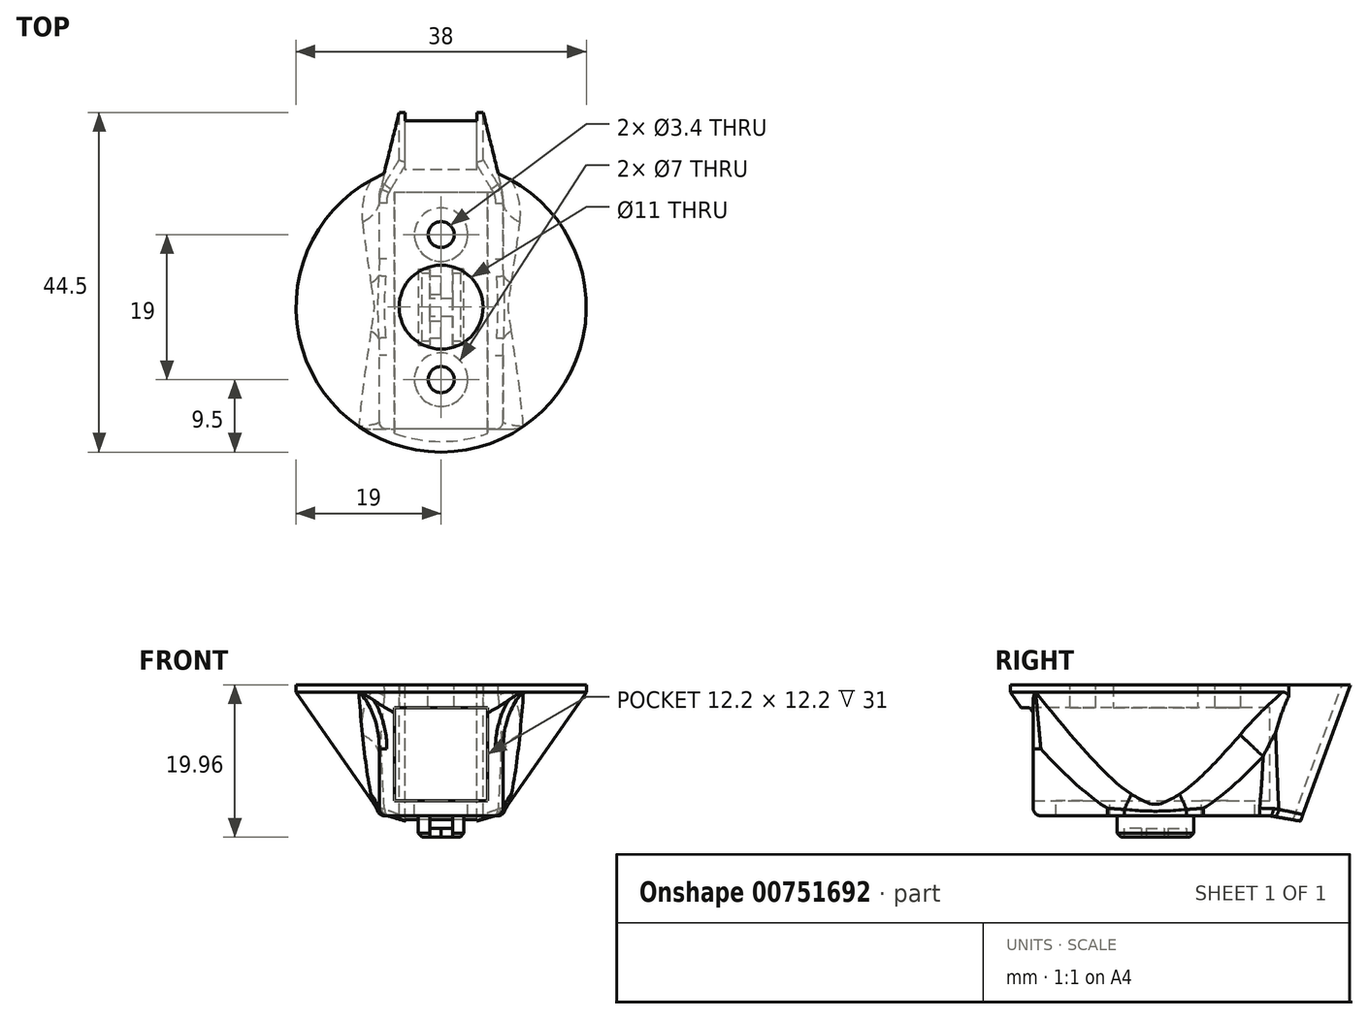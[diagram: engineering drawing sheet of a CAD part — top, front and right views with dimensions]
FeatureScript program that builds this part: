
annotation { "Feature Type Name" : "Feature", "Feature Type Description" : "" }
export const myFeature = defineFeature(function(context is Context, id is Id, definition is map)
    precondition{}
    {
        {
            var Q0;
            Q0=qCreatedBy(makeId("Front.planeOp"),FACE);
            var sketch = newSketch(context, id + "F0", { "sketchPlane" : qUnion([Q0])});
            skLineSegment(sketch, "E0", {"start": v(0, 1) * mm, "end": v(0, -16.2) * mm});
            skLineSegment(sketch, "E1", {"start": v(0, -16.2) * mm, "end": v(-7.76, -16.2) * mm});
            skLineSegment(sketch, "E2", {"start": v(-7.76, -16.2) * mm, "end": v(-19, 0) * mm});
            skLineSegment(sketch, "E3", {"start": v(-19, 0) * mm, "end": v(-19, 0.96) * mm});
            skLineSegment(sketch, "E4", {"start": v(-19, 0.96) * mm, "end": v(0, 1) * mm});
            skSolve(sketch);
        }
        {
            var Q0;
            Q0 = qSketchRegion(id + "F0", true);
            var Q1;
            Q1=sQuery(id+"F0.wireOp",EDGE,"E0");
            revolve(context, id + "F1", {"surfaceOperationType" : NewSurfaceOperationType.NEW, "entities" : qUnion([Q0]), "axis" : qUnion([Q1]), "revolveType" : RevolveType.FULL});
        }
        {
            var Q0;
            Q0=qCreatedBy(makeId("Top.planeOp"),FACE);
            var sketch = newSketch(context, id + "F2", { "sketchPlane" : qUnion([Q0])});
            skCircle(sketch, "E5", {"center": v(0, 9.5) * mm, "radius": 1.7 * mm});
            skCircle(sketch, "E6.MirrorC", {"center": v(0, -9.5) * mm, "radius": 1.7 * mm});
            skSolve(sketch);
        }
        {
            var Q0;
            Q0=qCreatedBy(makeId("Front.planeOp"),FACE);
            var sketch = newSketch(context, id + "F3", { "sketchPlane" : qUnion([Q0])});
            skLineSegment(sketch, "E7.bottom", {"start": v(6.1, -14.2) * mm, "end": v(-6.1, -14.2) * mm});
            skLineSegment(sketch, "E7.top", {"start": v(6.1, -2) * mm, "end": v(-6.1, -2) * mm});
            skLineSegment(sketch, "E7.left", {"start": v(6.1, -14.2) * mm, "end": v(6.1, -2) * mm});
            skLineSegment(sketch, "E7.right", {"start": v(-6.1, -14.2) * mm, "end": v(-6.1, -2) * mm});
            skPoint(sketch, "E7.middle", {"position": v(0, -8.1) * mm});
            skLineSegment(sketch, "E8.0", {"start": v(8.1, 0) * mm, "end": v(-8.1, 0) * mm});
            skLineSegment(sketch, "E8.1", {"start": v(8.1, -16.2) * mm, "end": v(8.1, 0) * mm});
            skLineSegment(sketch, "E8.2", {"start": v(8.1, -16.2) * mm, "end": v(-8.1, -16.2) * mm});
            skLineSegment(sketch, "E8.3", {"start": v(-8.1, -16.2) * mm, "end": v(-8.1, 0) * mm});
            skSolve(sketch);
        }
        {
            var Q0;
            Q0=makeQuery(id+"F3.imprint","IMPRINT",FACE,{"disambiguationData":[TD([[makeQuery(id+"F3.imprint","IMPRINT",EDGE,{"derivedFrom":sQuery(id+"F3.wireOp",EDGE,"E7.bottom")}),1.0]])]});
            extrude(context, id + "F4", {"entities" : qUnion([Q0]), "operationType" : NewBodyOperationType.ADD, "depth" : 16 * mm, "offsetDistance" : 25 * mm, "hasSecondDirection" : true, "secondDirectionOppositeDirection" : true, "secondDirectionDepth" : 15 * mm});
        }
        {
            var Q0;
            Q0=qCreatedBy(makeId("Front.planeOp"),FACE);
            var sketch = newSketch(context, id + "F5", { "sketchPlane" : qUnion([Q0])});
            skLineSegment(sketch, "E9.bottom", {"start": v(6.1, -14.2) * mm, "end": v(-6.1, -14.2) * mm});
            skLineSegment(sketch, "E9.top", {"start": v(6.1, -2) * mm, "end": v(-6.1, -2) * mm});
            skLineSegment(sketch, "E9.left", {"start": v(6.1, -14.2) * mm, "end": v(6.1, -2) * mm});
            skLineSegment(sketch, "E9.right", {"start": v(-6.1, -14.2) * mm, "end": v(-6.1, -2) * mm});
            skPoint(sketch, "E9.middle", {"position": v(0, -8.1) * mm});
            skSolve(sketch);
        }
        {
            var Q0;
            Q0 = qSketchRegion(id + "F5", true);
            extrude(context, id + "F6", {"entities" : qUnion([Q0]), "operationType" : NewBodyOperationType.REMOVE, "oppositeDirection" : true, "depth" : 25 * mm, "offsetDistance" : 25 * mm, "hasSecondDirection" : true, "secondDirectionOppositeDirection" : false, "secondDirectionDepth" : 25 * mm});
        }
        {
            var Q0;
            Q0 = qSketchRegion(id + "F2", true);
            var Q1;
            Q1=sQuery(id+"F2.wireOp",EDGE,"E5");
            var Q2;
            Q2=sQuery(id+"F2.wireOp",EDGE,"E6.MirrorC");
            extrude(context, id + "F7", {"entities" : qUnion([Q0]), "operationType" : NewBodyOperationType.REMOVE, "surfaceEntities" : qUnion([Q1, Q2]), "oppositeDirection" : true, "depth" : 25 * mm, "offsetDistance" : 25 * mm, "hasSecondDirection" : true, "secondDirectionOppositeDirection" : false, "secondDirectionDepth" : 25 * mm});
        }
        {
            var Q0;
            Q0=qCreatedBy(makeId("Top.planeOp"),FACE);
            var sketch = newSketch(context, id + "F8", { "sketchPlane" : qUnion([Q0])});
            skCircle(sketch, "E10", {"center": v(0, 9.5) * mm, "radius": 3.5 * mm});
            skCircle(sketch, "E11", {"center": v(0, -9.5) * mm, "radius": 3.5 * mm});
            skSolve(sketch);
        }
        {
            var Q0;
            Q0 = qSketchRegion(id + "F8", true);
            extrude(context, id + "F9", {"entities" : qUnion([Q0]), "operationType" : NewBodyOperationType.REMOVE, "oppositeDirection" : true, "depth" : 25 * mm, "offsetDistance" : 25 * mm, "hasSecondDirection" : true, "secondDirectionOppositeDirection" : true, "secondDirectionDepth" : 8.9 * mm});
        }
        {
            var Q0;
            Q0=qCreatedBy(makeId("Top.planeOp"),FACE);
            var sketch = newSketch(context, id + "F10", { "sketchPlane" : qUnion([Q0])});
            skCircle(sketch, "E12", {"center": v(0, 0) * mm, "radius": 5.5 * mm});
            skSolve(sketch);
        }
        {
            var Q0;
            Q0 = qSketchRegion(id + "F10", true);
            extrude(context, id + "F11", {"entities" : qUnion([Q0]), "operationType" : NewBodyOperationType.REMOVE, "depth" : 25 * mm, "offsetDistance" : 25 * mm, "hasSecondDirection" : true, "secondDirectionOppositeDirection" : true, "secondDirectionDepth" : 5 * mm});
        }
        {
            var Q0;
            Q0=makeQuery(id+"F4.opExtrude","CAP_EDGE",EDGE,{"disambiguationData":[OSD([sQuery(id+"F3.wireOp",EDGE,"E8.2")])],"isStart":true});
            cPlane(context, id + "F12", {"entities" : qUnion([Q0]), "cplaneType" : CPlaneType.LINE_ANGLE, "offset" : 25 * mm, "angle" : 20 * degree, "width" : 150 * mm, "height" : 150 * mm});
        }
        {
            var Q0;
            Q0=qCreatedBy(id+"F12.planeOp",FACE);
            cPlane(context, id + "F13", {"entities" : qUnion([Q0]), "cplaneType" : CPlaneType.OFFSET, "offset" : 4 * mm, "oppositeDirection" : true, "width" : 150 * mm, "height" : 150 * mm});
        }
        {
            var Q0;
            Q0=makeQuery(id+"F4.opExtrude","CAP_FACE",FACE,{"disambiguationData":[OSD([sQuery(id+"F3.wireOp",EDGE,"E7.bottom"),sQuery(id+"F3.wireOp",EDGE,"E7.top"),sQuery(id+"F3.wireOp",EDGE,"E7.left"),sQuery(id+"F3.wireOp",EDGE,"E7.right"),sQuery(id+"F3.wireOp",EDGE,"E8.0"),sQuery(id+"F3.wireOp",EDGE,"E8.1"),sQuery(id+"F3.wireOp",EDGE,"E8.2"),sQuery(id+"F3.wireOp",EDGE,"E8.3")])],"isStart":true});
            cPlane(context, id + "F14", {"entities" : qUnion([Q0]), "cplaneType" : CPlaneType.OFFSET, "offset" : 0 * mm, "width" : 150 * mm, "height" : 150 * mm});
        }
        {
            var Q0;
            Q0=qCreatedBy(id+"F13.planeOp",FACE);
            var sketch = newSketch(context, id + "F15", { "sketchPlane" : qUnion([Q0])});
            skLineSegment(sketch, "E13.bottom", {"start": v(-5.5, -9.38) * mm, "end": v(5.5, -9.38) * mm});
            skLineSegment(sketch, "E13.top", {"start": v(-5.5, 9.62) * mm, "end": v(5.5, 9.62) * mm});
            skLineSegment(sketch, "E13.left", {"start": v(-5.5, -9.38) * mm, "end": v(-5.5, 9.62) * mm});
            skLineSegment(sketch, "E13.right", {"start": v(5.5, -9.38) * mm, "end": v(5.5, 9.62) * mm});
            skPoint(sketch, "E13.middle", {"position": v(0, 0.72) * mm});
            skSolve(sketch);
        }
        {
            var Q0;
            Q0=qCreatedBy(id+"F14.planeOp",FACE);
            var sketch = newSketch(context, id + "F16", { "sketchPlane" : qUnion([Q0])});
            skLineSegment(sketch, "E14.bottom", {"start": v(-8.1, -16.2) * mm, "end": v(8.1, -16.2) * mm});
            skLineSegment(sketch, "E14.top", {"start": v(-8.1, 1.14) * mm, "end": v(8.1, 1.14) * mm});
            skLineSegment(sketch, "E14.left", {"start": v(-8.1, -16.2) * mm, "end": v(-8.1, 1.14) * mm});
            skLineSegment(sketch, "E14.right", {"start": v(8.1, -16.2) * mm, "end": v(8.1, 1.14) * mm});
            skSolve(sketch);
        }
        {
            var Q1;
            Q1 = qSketchRegion(id + "F15", true);
            var Q2;
            Q2 = qSketchRegion(id + "F16", true);
            loft(context, id + "F17", {"operationType" : NewBodyOperationType.ADD, "sheetProfilesArray" : [{ "sheetProfileEntities" : qUnion([Q1]) }, { "sheetProfileEntities" : qUnion([Q2]) }]});
        }
        {
            var Q0;
            Q0=qCreatedBy(makeId("Front.planeOp"),FACE);
            var sketch = newSketch(context, id + "F18", { "sketchPlane" : qUnion([Q0])});
            skLineSegment(sketch, "E15.bottom", {"start": v(19.79, 8.07) * mm, "end": v(-19.65, 8.07) * mm});
            skLineSegment(sketch, "E15.top", {"start": v(19.79, 0.96) * mm, "end": v(-19.65, 0.96) * mm});
            skLineSegment(sketch, "E15.left", {"start": v(19.79, 8.07) * mm, "end": v(19.79, 0.96) * mm});
            skLineSegment(sketch, "E15.right", {"start": v(-19.65, 8.07) * mm, "end": v(-19.65, 0.96) * mm});
            skSolve(sketch);
        }
        {
            var Q0;
            Q0 = qSketchRegion(id + "F18", true);
            extrude(context, id + "F19", {"entities" : qUnion([Q0]), "operationType" : NewBodyOperationType.REMOVE, "endBound" : BoundingType.SYMMETRIC, "oppositeDirection" : true, "depth" : 54.4 * mm, "offsetDistance" : 25 * mm});
        }
        {
            var Q0;
            Q0=qCreatedBy(id+"F13.planeOp",FACE);
            var sketch = newSketch(context, id + "F20", { "sketchPlane" : qUnion([Q0])});
            skPoint(sketch, "E16.middle", {"position": v(0, 0) * mm});
            skPoint(sketch, "E17.middle", {"position": v(0, -0.26) * mm});
            skLineSegment(sketch, "E18.bottom", {"start": v(-4.7, -11.6) * mm, "end": v(4.7, -11.6) * mm});
            skLineSegment(sketch, "E18.top", {"start": v(-4.7, 11.6) * mm, "end": v(4.7, 11.6) * mm});
            skLineSegment(sketch, "E18.left", {"start": v(-4.7, -11.6) * mm, "end": v(-4.7, 11.6) * mm});
            skLineSegment(sketch, "E18.right", {"start": v(4.7, -11.6) * mm, "end": v(4.7, 11.6) * mm});
            skSolve(sketch);
        }
        {
            var Q0;
            Q0 = qSketchRegion(id + "F20", true);
            extrude(context, id + "F21", {"entities" : qUnion([Q0]), "operationType" : NewBodyOperationType.REMOVE, "depth" : 1 * mm, "offsetDistance" : 25 * mm});
        }
        {
            var Q0;
            Q0=makeQuery(id+"F17.boolean.opBoolean","MERGE",EDGE,{"derivedFrom":[makeQuery(id+"F4.opExtrude","CAP_EDGE",EDGE,{"disambiguationData":[OSD([sQuery(id+"F3.wireOp",EDGE,"E8.1")])],"isStart":true}),makeQuery(id+"F17.opLoft","MID_CAP_EDGE",EDGE,{"disambiguationData":[OSD([sQuery(id+"F16.wireOp",EDGE,"E14.bottom"),sQuery(id+"F16.wireOp",EDGE,"E14.top"),sQuery(id+"F16.wireOp",EDGE,"E14.left")])],"capPos":1.0})]});
            var Q1;
            Q1=makeQuery(id+"F4.boolean.opBoolean","INTERSECT",EDGE,{"derivedFrom":[makeQuery(id+"F1.opRevolve","SWEPT_FACE",FACE,{"disambiguationData":[OSD([sQuery(id+"F0.wireOp",EDGE,"E2")])]}),makeQuery(id+"F4.opExtrude","SWEPT_FACE",FACE,{"disambiguationData":[OSD([sQuery(id+"F3.wireOp",EDGE,"E8.1")])]})]});
            var Q2;
            Q2=makeQuery(id+"F4.boolean.opBoolean","INTERSECT",EDGE,{"derivedFrom":[makeQuery(id+"F1.opRevolve","SWEPT_FACE",FACE,{"disambiguationData":[OSD([sQuery(id+"F0.wireOp",EDGE,"E2")])]}),makeQuery(id+"F4.opExtrude","SWEPT_FACE",FACE,{"disambiguationData":[OSD([sQuery(id+"F3.wireOp",EDGE,"E8.3")])]})]});
            var Q3;
            Q3=makeQuery(id+"F17.boolean.opBoolean","MERGE",EDGE,{"derivedFrom":[makeQuery(id+"F4.opExtrude","CAP_EDGE",EDGE,{"disambiguationData":[OSD([sQuery(id+"F3.wireOp",EDGE,"E8.3")])],"isStart":true}),makeQuery(id+"F17.opLoft","MID_CAP_EDGE",EDGE,{"disambiguationData":[OSD([sQuery(id+"F16.wireOp",EDGE,"E14.bottom"),sQuery(id+"F16.wireOp",EDGE,"E14.top"),sQuery(id+"F16.wireOp",EDGE,"E14.right")])],"capPos":1.0})]});
            fillet(context, id + "F22", {"entities" : qUnion([Q0, Q1, Q2, Q3]), "radius" : 5 * mm, "tangentPropagation" : true, "allowEdgeOverflow" : false});
        }
        {
            var Q0;
            Q0=makeQuery(id+"F4.opExtrude","SWEPT_EDGE",EDGE,{"disambiguationData":[OSD([sQuery(id+"F3.wireOp",EDGE,"E8.1"),sQuery(id+"F3.wireOp",EDGE,"E8.2")])]});
            var Q1;
            Q1=makeQuery(id+"F22.opFillet","BLEND_EDGE",EDGE,{"blendedFrom":[makeQuery(id+"F4.boolean.opBoolean","INTERSECT",EDGE,{"derivedFrom":[makeQuery(id+"F1.opRevolve","SWEPT_FACE",FACE,{"disambiguationData":[OSD([sQuery(id+"F0.wireOp",EDGE,"E2")])]}),makeQuery(id+"F4.opExtrude","SWEPT_FACE",FACE,{"disambiguationData":[OSD([sQuery(id+"F3.wireOp",EDGE,"E8.1")])]})]}),makeQuery(id+"F4.boolean.opBoolean","MERGE",FACE,{"derivedFrom":[makeQuery(id+"F1.opRevolve","SWEPT_FACE",FACE,{"disambiguationData":[OSD([sQuery(id+"F0.wireOp",EDGE,"E1")])]}),makeQuery(id+"F4.opExtrude","SWEPT_FACE",FACE,{"disambiguationData":[OSD([sQuery(id+"F3.wireOp",EDGE,"E8.2")])]})]})],"blendedInto":[makeQuery(id+"F4.boolean.opBoolean","MERGE",FACE,{"derivedFrom":[makeQuery(id+"F1.opRevolve","SWEPT_FACE",FACE,{"disambiguationData":[OSD([sQuery(id+"F0.wireOp",EDGE,"E1")])]}),makeQuery(id+"F4.opExtrude","SWEPT_FACE",FACE,{"disambiguationData":[OSD([sQuery(id+"F3.wireOp",EDGE,"E8.2")])]})]})]});
            var Q2;
            Q2=makeQuery(id+"F4.opExtrude","SWEPT_EDGE",EDGE,{"disambiguationData":[OSD([sQuery(id+"F3.wireOp",EDGE,"E8.1"),sQuery(id+"F3.wireOp",EDGE,"E8.2")])]});
            var Q3;
            Q3=makeQuery(id+"F4.opExtrude","CAP_EDGE",EDGE,{"disambiguationData":[OSD([sQuery(id+"F3.wireOp",EDGE,"E8.1")])],"isStart":false});
            var Q4;
            Q4=makeQuery(id+"F4.opExtrude","CAP_EDGE",EDGE,{"disambiguationData":[OSD([sQuery(id+"F3.wireOp",EDGE,"E8.2")])],"isStart":false});
            var Q5;
            Q5=makeQuery(id+"F4.opExtrude","CAP_EDGE",EDGE,{"disambiguationData":[OSD([sQuery(id+"F3.wireOp",EDGE,"E8.3")])],"isStart":false});
            var Q6;
            Q6=makeQuery(id+"F4.opExtrude","SWEPT_EDGE",EDGE,{"disambiguationData":[OSD([sQuery(id+"F3.wireOp",EDGE,"E8.2"),sQuery(id+"F3.wireOp",EDGE,"E8.3")])]});
            var Q7;
            Q7=makeQuery(id+"F4.opExtrude","SWEPT_EDGE",EDGE,{"disambiguationData":[OSD([sQuery(id+"F3.wireOp",EDGE,"E8.2"),sQuery(id+"F3.wireOp",EDGE,"E8.3")])]});
            var Q8;
            Q8=makeQuery(id+"F22.opFillet","BLEND_EDGE",EDGE,{"blendedFrom":[makeQuery(id+"F4.boolean.opBoolean","INTERSECT",EDGE,{"derivedFrom":[makeQuery(id+"F1.opRevolve","SWEPT_FACE",FACE,{"disambiguationData":[OSD([sQuery(id+"F0.wireOp",EDGE,"E2")])]}),makeQuery(id+"F4.opExtrude","SWEPT_FACE",FACE,{"disambiguationData":[OSD([sQuery(id+"F3.wireOp",EDGE,"E8.3")])]})]}),makeQuery(id+"F4.boolean.opBoolean","MERGE",FACE,{"derivedFrom":[makeQuery(id+"F1.opRevolve","SWEPT_FACE",FACE,{"disambiguationData":[OSD([sQuery(id+"F0.wireOp",EDGE,"E1")])]}),makeQuery(id+"F4.opExtrude","SWEPT_FACE",FACE,{"disambiguationData":[OSD([sQuery(id+"F3.wireOp",EDGE,"E8.2")])]})]})],"blendedInto":[makeQuery(id+"F4.boolean.opBoolean","MERGE",FACE,{"derivedFrom":[makeQuery(id+"F1.opRevolve","SWEPT_FACE",FACE,{"disambiguationData":[OSD([sQuery(id+"F0.wireOp",EDGE,"E1")])]}),makeQuery(id+"F4.opExtrude","SWEPT_FACE",FACE,{"disambiguationData":[OSD([sQuery(id+"F3.wireOp",EDGE,"E8.2")])]})]})]});
            var Q9;
            Q9=makeQuery(id+"F17.opLoft","SWEPT_EDGE",EDGE,{"disambiguationData":[OSD([sQuery(id+"F15.wireOp",EDGE,"E13.bottom"),sQuery(id+"F15.wireOp",EDGE,"E13.right"),sQuery(id+"F16.wireOp",EDGE,"E14.bottom"),sQuery(id+"F16.wireOp",EDGE,"E14.left")])]});
            var Q10;
            {var subQ0=sQuery(id+"F16.wireOp",EDGE,"E14.left");var subQ1=sQuery(id+"F16.wireOp",EDGE,"E14.bottom");Q10=makeQuery(id+"F22.opFillet","BLEND_EDGE",EDGE,{"blendedFrom":[makeQuery(id+"F17.boolean.opBoolean","MERGE",EDGE,{"derivedFrom":[makeQuery(id+"F4.opExtrude","CAP_EDGE",EDGE,{"disambiguationData":[OSD([sQuery(id+"F3.wireOp",EDGE,"E8.1")])],"isStart":true}),makeQuery(id+"F17.opLoft","MID_CAP_EDGE",EDGE,{"disambiguationData":[OSD([subQ1,sQuery(id+"F16.wireOp",EDGE,"E14.top"),subQ0])],"capPos":1.0})]}),makeQuery(id+"F17.opLoft","SWEPT_FACE",FACE,{"disambiguationData":[OSD([sQuery(id+"F15.wireOp",EDGE,"E13.bottom"),sQuery(id+"F15.wireOp",EDGE,"E13.left"),sQuery(id+"F15.wireOp",EDGE,"E13.right"),subQ1,subQ0,sQuery(id+"F16.wireOp",EDGE,"E14.right")])]})],"blendedInto":[makeQuery(id+"F17.opLoft","SWEPT_FACE",FACE,{"disambiguationData":[OSD([sQuery(id+"F15.wireOp",EDGE,"E13.bottom"),sQuery(id+"F15.wireOp",EDGE,"E13.left"),sQuery(id+"F15.wireOp",EDGE,"E13.right"),subQ1,subQ0,sQuery(id+"F16.wireOp",EDGE,"E14.right")])]})]});}
            var Q11;
            Q11=makeQuery(id+"F17.opLoft","SWEPT_EDGE",EDGE,{"disambiguationData":[OSD([sQuery(id+"F15.wireOp",EDGE,"E13.bottom"),sQuery(id+"F15.wireOp",EDGE,"E13.left"),sQuery(id+"F16.wireOp",EDGE,"E14.bottom"),sQuery(id+"F16.wireOp",EDGE,"E14.right")])]});
            fillet(context, id + "F23", {"entities" : qUnion([Q0, Q1, Q2, Q3, Q4, Q5, Q6, Q7, Q8, Q9, Q10, Q11]), "radius" : 1 * mm, "tangentPropagation" : true, "allowEdgeOverflow" : false});
        }
        {
            var Q0;
            Q0=qCreatedBy(makeId("Top.planeOp"),FACE);
            var sketch = newSketch(context, id + "F24", { "sketchPlane" : qUnion([Q0])});
            skLineSegment(sketch, "E19", {"start": v(0, 0) * mm, "end": v(0, -10.57) * mm, "construction": true});
            skLineSegment(sketch, "E20", {"start": v(0, 0) * mm, "end": v(-1.5, 0) * mm});
            skLineSegment(sketch, "E21.bottom", {"start": v(-1.5, 0) * mm, "end": v(-3, 0) * mm});
            skLineSegment(sketch, "E21.top", {"start": v(-1.5, 5) * mm, "end": v(-3, 5) * mm});
            skLineSegment(sketch, "E21.left", {"start": v(-1.5, 0) * mm, "end": v(-1.5, 5) * mm});
            skLineSegment(sketch, "E21.right", {"start": v(-3, 0) * mm, "end": v(-3, 5) * mm});
            skLineSegment(sketch, "E22.top", {"start": v(-1.5, -5) * mm, "end": v(-3, -5) * mm});
            skLineSegment(sketch, "E22.left", {"start": v(-1.5, 0) * mm, "end": v(-1.5, -5) * mm});
            skLineSegment(sketch, "E22.right", {"start": v(-3, 0) * mm, "end": v(-3, -5) * mm});
            skLineSegment(sketch, "E23.MirrorCS", {"start": v(1.5, 0) * mm, "end": v(3, 0) * mm});
            skLineSegment(sketch, "E24.MirrorCS", {"start": v(1.5, 0) * mm, "end": v(1.5, -5) * mm});
            skLineSegment(sketch, "E25.MirrorCS", {"start": v(1.5, -5) * mm, "end": v(3, -5) * mm});
            skLineSegment(sketch, "E26.MirrorCS", {"start": v(3, 0) * mm, "end": v(3, 5) * mm});
            skLineSegment(sketch, "E27.MirrorCS", {"start": v(1.5, 0) * mm, "end": v(1.5, 5) * mm});
            skLineSegment(sketch, "E28.MirrorCS", {"start": v(3, 0) * mm, "end": v(3, -5) * mm});
            skLineSegment(sketch, "E29.MirrorCS", {"start": v(1.5, 5) * mm, "end": v(3, 5) * mm});
            skSolve(sketch);
        }
        {
            var Q0;
            Q0 = qSketchRegion(id + "F24", true);
            var Q1;
            Q1=makeQuery(id+"F4.boolean.opBoolean","MERGE",FACE,{"derivedFrom":[makeQuery(id+"F1.opRevolve","SWEPT_FACE",FACE,{"disambiguationData":[OSD([sQuery(id+"F0.wireOp",EDGE,"E1")])]}),makeQuery(id+"F4.opExtrude","SWEPT_FACE",FACE,{"disambiguationData":[OSD([sQuery(id+"F3.wireOp",EDGE,"E8.2")])]})]});
            extrude(context, id + "F25", {"entities" : qUnion([Q0]), "operationType" : NewBodyOperationType.ADD, "oppositeDirection" : true, "depth" : 19 * mm, "offsetDistance" : 25 * mm, "hasSecondDirection" : true, "secondDirectionBound" : SecondDirectionBoundingType.UP_TO_SURFACE, "secondDirectionOppositeDirection" : true, "secondDirectionDepth" : 16.1 * mm, "secondDirectionBoundEntityFace" : qUnion([Q1])});
        }
        {
            var Q0;
            Q0=makeQuery(id+"F25.opExtrude","CAP_EDGE",EDGE,{"disambiguationData":[OSD([sQuery(id+"F24.wireOp",EDGE,"E21.right"),sQuery(id+"F24.wireOp",EDGE,"E22.right")])],"isStart":false});
            var Q1;
            Q1=makeQuery(id+"F25.opExtrude","CAP_EDGE",EDGE,{"disambiguationData":[OSD([sQuery(id+"F24.wireOp",EDGE,"E26.MirrorCS"),sQuery(id+"F24.wireOp",EDGE,"E28.MirrorCS")])],"isStart":false});
            var Q2;
            Q2=makeQuery(id+"F25.opExtrude","CAP_EDGE",EDGE,{"disambiguationData":[OSD([sQuery(id+"F24.wireOp",EDGE,"E25.MirrorCS")])],"isStart":false});
            var Q3;
            Q3=makeQuery(id+"F25.opExtrude","CAP_EDGE",EDGE,{"disambiguationData":[OSD([sQuery(id+"F24.wireOp",EDGE,"E22.top")])],"isStart":false});
            var Q4;
            Q4=makeQuery(id+"F25.opExtrude","CAP_EDGE",EDGE,{"disambiguationData":[OSD([sQuery(id+"F24.wireOp",EDGE,"E21.top")])],"isStart":false});
            var Q5;
            Q5=makeQuery(id+"F25.opExtrude","CAP_EDGE",EDGE,{"disambiguationData":[OSD([sQuery(id+"F24.wireOp",EDGE,"E29.MirrorCS")])],"isStart":false});
            chamfer(context, id + "F26", {"entities" : qUnion([Q0, Q1, Q2, Q3, Q4, Q5]), "width" : .5 * mm, "tangentPropagation" : true});
        }
        {
            var Q0;
            Q0=makeQuery(id+"F25.opExtrude","SWEPT_FACE",FACE,{"disambiguationData":[OSD([sQuery(id+"F24.wireOp",EDGE,"E21.left"),sQuery(id+"F24.wireOp",EDGE,"E22.left")])]});
            var sketch = newSketch(context, id + "F27", { "sketchPlane" : qUnion([Q0])});
            skLineSegment(sketch, "E30.bottom", {"start": v(-1.23, -17.86) * mm, "end": v(1.12, -17.86) * mm});
            skLineSegment(sketch, "E30.top", {"start": v(-1.23, -19) * mm, "end": v(1.12, -19) * mm});
            skLineSegment(sketch, "E30.left", {"start": v(-1.23, -17.86) * mm, "end": v(-1.23, -19) * mm});
            skLineSegment(sketch, "E30.right", {"start": v(1.12, -17.86) * mm, "end": v(1.12, -19) * mm});
            skLineSegment(sketch, "E31.bottom", {"start": v(1.62, -17.86) * mm, "end": v(4.05, -17.86) * mm});
            skLineSegment(sketch, "E31.top", {"start": v(1.62, -19) * mm, "end": v(4.05, -19) * mm});
            skLineSegment(sketch, "E31.left", {"start": v(1.62, -17.86) * mm, "end": v(1.62, -19) * mm});
            skLineSegment(sketch, "E31.right", {"start": v(4.05, -17.86) * mm, "end": v(4.05, -19) * mm});
            skLineSegment(sketch, "E32.bottom", {"start": v(-1.87, -17.86) * mm, "end": v(-4.12, -17.86) * mm});
            skLineSegment(sketch, "E32.top", {"start": v(-1.87, -19) * mm, "end": v(-4.12, -19) * mm});
            skLineSegment(sketch, "E32.left", {"start": v(-1.87, -17.86) * mm, "end": v(-1.87, -19) * mm});
            skLineSegment(sketch, "E32.right", {"start": v(-4.12, -17.86) * mm, "end": v(-4.12, -19) * mm});
            skSolve(sketch);
        }
        {
            var Q0;
            Q0=makeQuery(id+"F27.imprint","IMPRINT",FACE,{"disambiguationData":[TD([[makeQuery(id+"F27.imprint","IMPRINT",EDGE,{"derivedFrom":sQuery(id+"F27.wireOp",EDGE,"E31.bottom")}),-1.0]])]});
            var Q1;
            Q1=makeQuery(id+"F27.imprint","IMPRINT",FACE,{"disambiguationData":[TD([[makeQuery(id+"F27.imprint","IMPRINT",EDGE,{"derivedFrom":sQuery(id+"F27.wireOp",EDGE,"E32.bottom")}),1.0]])]});
            extrude(context, id + "F28", {"entities" : qUnion([Q0, Q1]), "operationType" : NewBodyOperationType.ADD, "depth" : 1.5 * mm, "offsetDistance" : 25 * mm});
        }
        {
            var Q0;
            Q0=makeQuery(id+"F27.imprint","IMPRINT",FACE,{"disambiguationData":[TD([[makeQuery(id+"F27.imprint","IMPRINT",EDGE,{"derivedFrom":sQuery(id+"F27.wireOp",EDGE,"E30.bottom")}),-1.0]])]});
            var Q1;
            Q1=makeQuery(id+"F25.opExtrude","SWEPT_FACE",FACE,{"disambiguationData":[OSD([sQuery(id+"F24.wireOp",EDGE,"E24.MirrorCS"),sQuery(id+"F24.wireOp",EDGE,"E27.MirrorCS")])]});
            extrude(context, id + "F29", {"entities" : qUnion([Q0]), "operationType" : NewBodyOperationType.ADD, "endBound" : BoundingType.UP_TO_SURFACE, "depth" : 25 * mm, "endBoundEntityFace" : qUnion([Q1]), "offsetDistance" : 25 * mm, "hasSecondDirection" : true, "secondDirectionOppositeDirection" : true, "secondDirectionDepth" : -2 * mm});
        }
        {
            var Q0;
            Q0=makeQuery(id+"F27.imprint","IMPRINT",FACE,{"disambiguationData":[TD([[makeQuery(id+"F27.imprint","IMPRINT",EDGE,{"derivedFrom":sQuery(id+"F27.wireOp",EDGE,"E30.bottom")}),-1.0]])]});
            var Q1;
            Q1=makeQuery(id+"F25.opExtrude","SWEPT_FACE",FACE,{"disambiguationData":[OSD([sQuery(id+"F24.wireOp",EDGE,"E24.MirrorCS"),sQuery(id+"F24.wireOp",EDGE,"E27.MirrorCS")])]});
            extrude(context, id + "F30", {"entities" : qUnion([Q0]), "operationType" : NewBodyOperationType.ADD, "endBound" : BoundingType.UP_TO_SURFACE, "depth" : 25 * mm, "endBoundEntityFace" : qUnion([Q1]), "offsetDistance" : 25 * mm});
        }
    });
